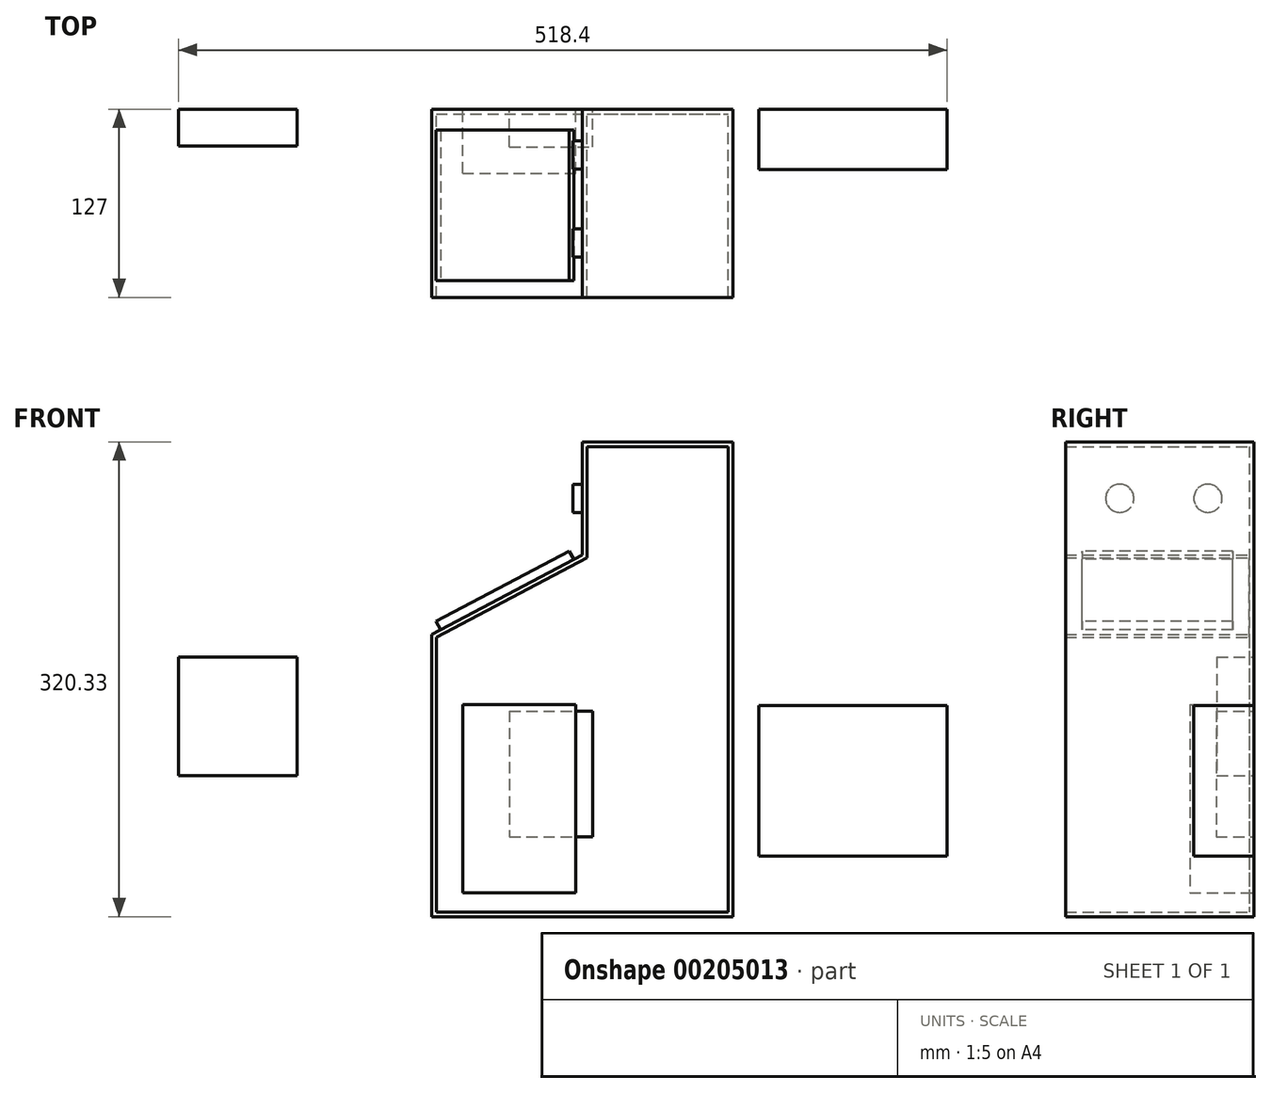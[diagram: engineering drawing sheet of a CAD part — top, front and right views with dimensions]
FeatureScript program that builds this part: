
annotation { "Feature Type Name" : "Feature", "Feature Type Description" : "" }
export const myFeature = defineFeature(function(context is Context, id is Id, definition is map)
    precondition{}
    {
        {
            var Q0;
            Q0=qCreatedBy(makeId("Front.planeOp"),FACE);
            var sketch = newSketch(context, id + "F0", { "sketchPlane" : qUnion([Q0])});
            skLineSegment(sketch, "E0.top", {"start": v(-69.46, -126.2) * mm, "end": v(133.74, -126.2) * mm});
            skLineSegment(sketch, "E0.left", {"start": v(-69.46, 64.3) * mm, "end": v(-69.46, -126.2) * mm});
            skLineSegment(sketch, "E0.right", {"start": v(133.74, 105.58) * mm, "end": v(133.74, -126.2) * mm});
            skLineSegment(sketch, "E1.bottom", {"start": v(32.14, 194.13) * mm, "end": v(133.74, 194.13) * mm});
            skLineSegment(sketch, "E1.left", {"start": v(32.14, 194.13) * mm, "end": v(32.14, 117.93) * mm});
            skLineSegment(sketch, "E1.right", {"start": v(133.74, 194.13) * mm, "end": v(133.74, 105.58) * mm});
            skLineSegment(sketch, "E2", {"start": v(-69.46, 64.3) * mm, "end": v(32.14, 117.93) * mm});
            skLineSegment(sketch, "E3.0", {"start": v(-66.28, 62.39) * mm, "end": v(35.32, 116.01) * mm});
            skLineSegment(sketch, "E3.1", {"start": v(35.32, 190.95) * mm, "end": v(35.32, 116.01) * mm});
            skLineSegment(sketch, "E3.2", {"start": v(-66.28, -123.02) * mm, "end": v(130.57, -123.02) * mm});
            skLineSegment(sketch, "E3.3", {"start": v(130.57, 105.58) * mm, "end": v(130.57, -123.02) * mm});
            skLineSegment(sketch, "E3.4", {"start": v(130.57, 190.95) * mm, "end": v(130.57, 105.58) * mm});
            skLineSegment(sketch, "E3.5", {"start": v(-66.28, 62.39) * mm, "end": v(-66.28, -123.02) * mm});
            skLineSegment(sketch, "E3.6", {"start": v(35.32, 190.95) * mm, "end": v(130.57, 190.95) * mm});
            skPoint(sketch, "E4", {"position": v(130.57, -8.72) * mm});
            skSolve(sketch);
        }
        {
            var Q0;
            Q0=makeQuery(id+"F0.imprint","IMPRINT",FACE,{"disambiguationData":[TD([[makeQuery(id+"F0.imprint","IMPRINT",EDGE,{"derivedFrom":sQuery(id+"F0.wireOp",EDGE,"E0.top")}),1.0]])]});
            extrude(context, id + "F1", {"entities" : qUnion([Q0]), "depth" : 127 * mm});
        }
        {
            var Q0;
            Q0=makeQuery(id+"F0.imprint","IMPRINT",FACE,{"disambiguationData":[TD([[makeQuery(id+"F0.imprint","IMPRINT",EDGE,{"derivedFrom":sQuery(id+"F0.wireOp",EDGE,"E3.0")}),-1.0]])]});
            extrude(context, id + "F2", {"entities" : qUnion([Q0]), "operationType" : NewBodyOperationType.ADD, "depth" : 3.17 * mm});
        }
        {
            var Q0;
            Q0=qCreatedBy(makeId("Front.planeOp"),FACE);
            var sketch = newSketch(context, id + "F3", { "sketchPlane" : qUnion([Q0])});
            skLineSegment(sketch, "E5.bottom", {"start": v(-16.96, 12.54) * mm, "end": v(39.04, 12.54) * mm});
            skLineSegment(sketch, "E5.top", {"start": v(-16.96, -72.46) * mm, "end": v(39.04, -72.46) * mm});
            skLineSegment(sketch, "E5.left", {"start": v(-16.96, 12.54) * mm, "end": v(-16.96, -72.46) * mm});
            skLineSegment(sketch, "E5.right", {"start": v(39.04, 12.54) * mm, "end": v(39.04, -72.46) * mm});
            skSolve(sketch);
        }
        {
            var Q0;
            Q0=makeQuery(id+"F3.imprint","IMPRINT",FACE,{"disambiguationData":[TD([[makeQuery(id+"F3.imprint","IMPRINT",EDGE,{"derivedFrom":sQuery(id+"F3.wireOp",EDGE,"E5.bottom")}),-1.0]])]});
            extrude(context, id + "F4", {"entities" : qUnion([Q0]), "depth" : 25.4 * mm});
        }
        {
            var Q0;
            Q0=qCreatedBy(makeId("Front.planeOp"),FACE);
            var sketch = newSketch(context, id + "F5", { "sketchPlane" : qUnion([Q0])});
            skLineSegment(sketch, "E6.bottom", {"start": v(-48.58, 16.76) * mm, "end": v(27.62, 16.76) * mm});
            skLineSegment(sketch, "E6.top", {"start": v(-48.58, -110.24) * mm, "end": v(27.62, -110.24) * mm});
            skLineSegment(sketch, "E6.left", {"start": v(-48.58, 16.76) * mm, "end": v(-48.58, -110.24) * mm});
            skLineSegment(sketch, "E6.right", {"start": v(27.62, 16.76) * mm, "end": v(27.62, -110.24) * mm});
            skSolve(sketch);
        }
        {
            var Q0;
            Q0 = qSketchRegion(id + "F5", true);
            extrude(context, id + "F6", {"entities" : qUnion([Q0]), "depth" : 43.18 * mm});
        }
        {
            var Q0;
            Q0=qCreatedBy(makeId("Front.planeOp"),FACE);
            var sketch = newSketch(context, id + "F7", { "sketchPlane" : qUnion([Q0])});
            skLineSegment(sketch, "E7.bottom", {"start": v(151.2, 16.13) * mm, "end": v(278.2, 16.13) * mm});
            skLineSegment(sketch, "E7.top", {"start": v(151.2, -85.47) * mm, "end": v(278.2, -85.47) * mm});
            skLineSegment(sketch, "E7.left", {"start": v(151.2, 16.13) * mm, "end": v(151.2, -85.47) * mm});
            skLineSegment(sketch, "E7.right", {"start": v(278.2, 16.13) * mm, "end": v(278.2, -85.47) * mm});
            skSolve(sketch);
        }
        {
            var Q0;
            Q0 = qSketchRegion(id + "F7", true);
            extrude(context, id + "F8", {"entities" : qUnion([Q0]), "depth" : 40.64 * mm});
        }
        {
            var Q0;
            Q0=qCreatedBy(makeId("Front.planeOp"),FACE);
            var sketch = newSketch(context, id + "F9", { "sketchPlane" : qUnion([Q0])});
            skLineSegment(sketch, "E8.bottom", {"start": v(-240.2, 49.01) * mm, "end": v(-160.2, 49.01) * mm});
            skLineSegment(sketch, "E8.top", {"start": v(-240.2, -30.99) * mm, "end": v(-160.2, -30.99) * mm});
            skLineSegment(sketch, "E8.left", {"start": v(-240.2, 49.01) * mm, "end": v(-240.2, -30.99) * mm});
            skLineSegment(sketch, "E8.right", {"start": v(-160.2, 49.01) * mm, "end": v(-160.2, -30.99) * mm});
            skSolve(sketch);
        }
        {
            var Q0;
            Q0=makeQuery(id+"F9.imprint","IMPRINT",FACE,{"disambiguationData":[TD([[makeQuery(id+"F9.imprint","IMPRINT",EDGE,{"derivedFrom":sQuery(id+"F9.wireOp",EDGE,"E8.bottom")}),-1.0]])]});
            extrude(context, id + "F10", {"entities" : qUnion([Q0]), "depth" : 25 * mm});
        }
        {
            var Q0;
            Q0=makeQuery(id+"F1.opExtrude","SWEPT_FACE",FACE,{"disambiguationData":[OSD([sQuery(id+"F0.wireOp",EDGE,"E2")])]});
            var sketch = newSketch(context, id + "F11", { "sketchPlane" : qUnion([Q0])});
            skLineSegment(sketch, "E9.bottom", {"start": v(-24.66, -14.21) * mm, "end": v(76.94, -14.21) * mm});
            skLineSegment(sketch, "E9.top", {"start": v(-24.66, -115.81) * mm, "end": v(76.94, -115.81) * mm});
            skLineSegment(sketch, "E9.left", {"start": v(-24.66, -14.21) * mm, "end": v(-24.66, -115.81) * mm});
            skLineSegment(sketch, "E9.right", {"start": v(76.94, -14.21) * mm, "end": v(76.94, -115.81) * mm});
            skSolve(sketch);
        }
        {
            var Q0;
            Q0=makeQuery(id+"F11.imprint","IMPRINT",FACE,{"disambiguationData":[TD([[makeQuery(id+"F11.imprint","IMPRINT",EDGE,{"derivedFrom":sQuery(id+"F11.wireOp",EDGE,"E9.bottom")}),-1.0]])]});
            extrude(context, id + "F12", {"entities" : qUnion([Q0]), "operationType" : NewBodyOperationType.ADD, "depth" : 6.35 * mm});
        }
        {
            var Q0;
            Q0=makeQuery(id+"F1.opExtrude","SWEPT_FACE",FACE,{"disambiguationData":[OSD([sQuery(id+"F0.wireOp",EDGE,"E1.left")])]});
            var sketch = newSketch(context, id + "F13", { "sketchPlane" : qUnion([Q0])});
            skPoint(sketch, "E10", {"position": v(30.97, 156.03) * mm});
            skPoint(sketch, "E10.positionSnap0", {"position": v(0, 156.03) * mm});
            skPoint(sketch, "E11", {"position": v(127, 156.03) * mm});
            skPoint(sketch, "E12", {"position": v(90.4, 156.03) * mm});
            skCircle(sketch, "E13", {"center": v(30.97, 156.03) * mm, "radius": 9.53 * mm});
            skCircle(sketch, "E14", {"center": v(90.4, 156.03) * mm, "radius": 9.53 * mm});
            skSolve(sketch);
        }
        {
            var Q0;
            Q0=makeQuery(id+"F13.imprint","IMPRINT",FACE,{"disambiguationData":[TD([[makeQuery(id+"F13.imprint","IMPRINT",EDGE,{"derivedFrom":sQuery(id+"F13.wireOp",EDGE,"E13")}),1.0]])]});
            var Q1;
            Q1=makeQuery(id+"F13.imprint","IMPRINT",FACE,{"disambiguationData":[TD([[makeQuery(id+"F13.imprint","IMPRINT",EDGE,{"derivedFrom":sQuery(id+"F13.wireOp",EDGE,"E14")}),1.0]])]});
            extrude(context, id + "F14", {"entities" : qUnion([Q0, Q1]), "operationType" : NewBodyOperationType.ADD, "depth" : 6.35 * mm});
        }
    });
